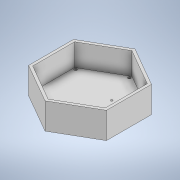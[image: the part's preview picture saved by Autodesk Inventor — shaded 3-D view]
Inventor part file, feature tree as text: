
AUTODESK INVENTOR PART (.ipt)
format: ipt  version: 2020 (Build 240168000, 168)  size: 226,816 bytes
history: native  units: mm
features: extrude x5, sketch x3
ambient origin geometry x8: Origin, YZ Plane, XZ Plane, XY Plane, X Axis, Y Axis, Z Axis, Center Point
bodies: Solid1 (feature_tree)
feature tree (8):
  sketch  "Sketch1"  dims[d1=80.0mm d2=80.0mm]
  extrude  "Extrusion1"  Depth=80.0mm
  extrude  "Extrusion2"  Depth=80.0mm
  extrude  "Extrusion3"  TaperAngle=120.0deg  [1 undecoded]
  sketch  "Sketch3"  dims[d5=80.0mm d6=120.0deg d7=120.0deg d9=120.0deg d10=120.0deg d11=120.0deg d15=5.0mm d16=148.564065mm d18=0.0mm d20=0.0mm d22=3.81mm d23=41.91mm d24=4.45mm d25=44.485mm d26=3.81mm d27=3.81mm d28=41.91mm d29=44.485mm d30=1.0mm d31=19.045mm d32=5.0mm d33=0.0mm d35=5.0mm d36=150.0deg d37=5.0mm d38=90.0deg d39=5.0mm d40=30.0deg d42=5.0mm d43=5.0mm d44=5.0mm d45=60.0deg d47=5.0mm d48=5.0mm d49=60.0deg d50=5.0mm d51=5.0mm d52=5.0mm d53=2.5mm d54=2.5mm d55=2.5mm d56=2.5mm d57=2.5mm d58=2.5mm d59=3.75mm d60=0.0mm d61=7.5mm d62=0.0mm]
  extrude  "Extrusion4"  TaperAngle=120.0deg  [1 undecoded]
  extrude  "Extrusion5"  TaperAngle=120.0deg  [1 undecoded]
  sketch  "Sketch2"  dims[d3=80.0mm d4=80.0mm]
note: 3 required parameter values undecoded (feature->parameter linkage not recoverable at this tier; creation-order binding heuristic only, values carry confidence <= 0.55)
